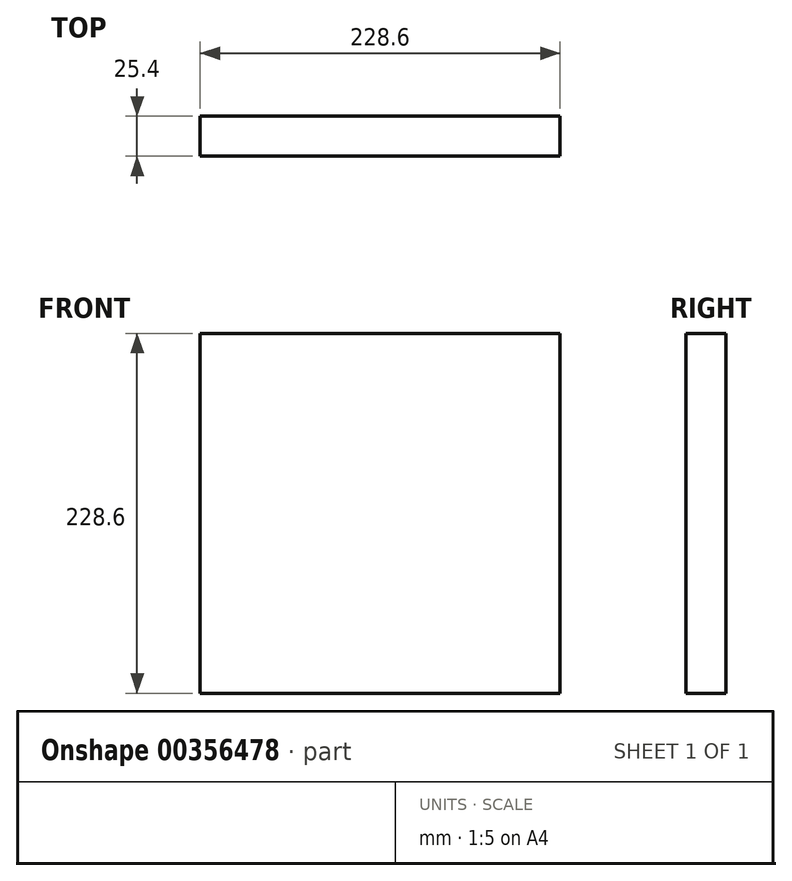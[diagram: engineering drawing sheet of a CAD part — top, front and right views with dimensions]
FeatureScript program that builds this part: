
annotation { "Feature Type Name" : "Feature", "Feature Type Description" : "" }
export const myFeature = defineFeature(function(context is Context, id is Id, definition is map)
    precondition{}
    {
        {
            var Q0;
            Q0=qCreatedBy(makeId("Front.planeOp"),FACE);
            var sketch = newSketch(context, id + "F0", { "sketchPlane" : qUnion([Q0])});
            skLineSegment(sketch, "E0.bottom", {"start": v(-46.86, 179.88) * mm, "end": v(181.74, 179.88) * mm});
            skLineSegment(sketch, "E0.top", {"start": v(-46.86, -48.72) * mm, "end": v(181.74, -48.72) * mm});
            skLineSegment(sketch, "E0.left", {"start": v(-46.86, 179.88) * mm, "end": v(-46.86, -48.72) * mm});
            skLineSegment(sketch, "E0.right", {"start": v(181.74, 179.88) * mm, "end": v(181.74, -48.72) * mm});
            skSolve(sketch);
        }
        {
            var Q0;
            Q0=makeQuery(id+"F0.imprint","IMPRINT",FACE,{"disambiguationData":[TD([[makeQuery(id+"F0.imprint","IMPRINT",EDGE,{"derivedFrom":sQuery(id+"F0.wireOp",EDGE,"E0.bottom")}),-1.0]])]});
            extrude(context, id + "F1", {"entities" : qUnion([Q0]), "depth" : 25.4 * mm});
        }
    });
